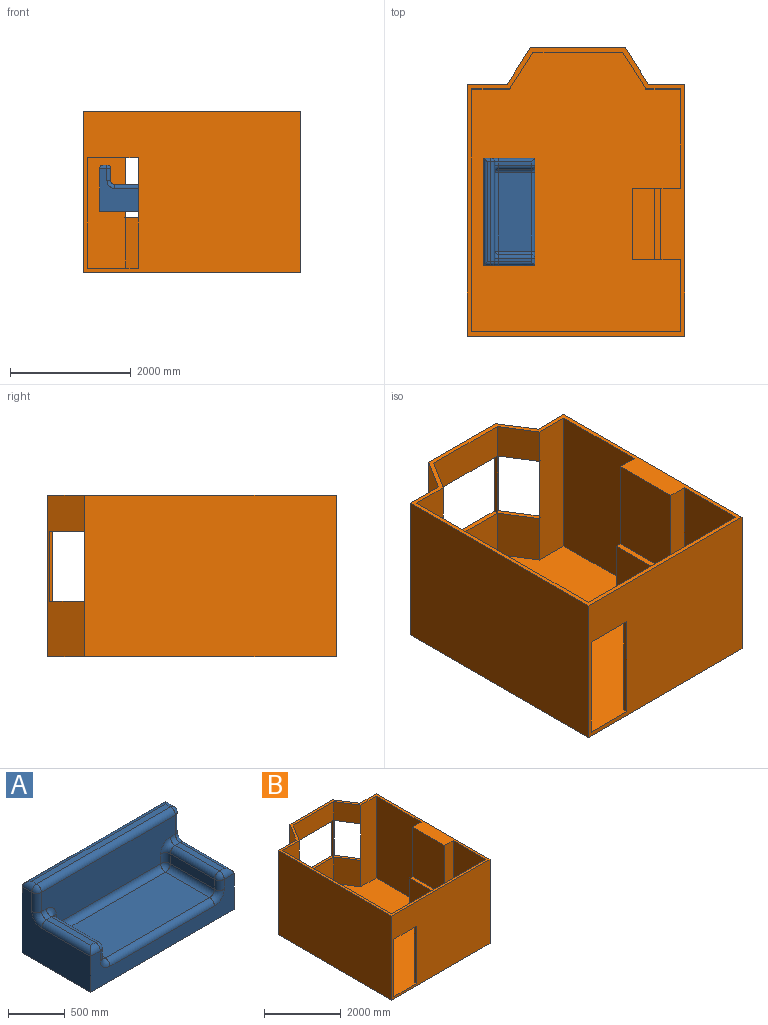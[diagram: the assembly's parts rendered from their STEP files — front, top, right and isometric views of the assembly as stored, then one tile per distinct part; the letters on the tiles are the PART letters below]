
ASSEMBLY  parts=2 mates=1
PART A: 46 faces, bbox 1780x850x770 mm
  f0: plane 1660x430.77mm, normal (0,-1,0), area 639255.4mm2, adj f17,f18,f22,f26,f30,f34,f38,f39
  f1: plane 548.57x61.43mm, normal (0,0,1), area 33697.9mm2, adj f13,f19,f22,f23
  f2: plane 1780x385.23mm, normal (0,-1,0), area 344493.1mm2, adj f3,f6,f7,f12,f15,f19,f20,f24
  f3: plane 1780x850mm, normal (0,0,-1), area 1513000mm2, adj f2,f4,f6,f7
  f4: plane 1780x710mm, normal (0,1,0), area 1263800mm2, adj f3,f6,f7,f36
  f5: plane 1660x61.43mm, normal (0,0,1), area 101971.3mm2, adj f31,f36,f39,f40
  f6: plane 850x710mm, normal (1,0,0), area 369971.1mm2, adj f2,f3,f4,f40,f41,f44,f45
  f7: plane 850x710mm, normal (-1,0,0), area 369971.1mm2, adj f2,f3,f4,f23,f27,f30,f31
  f8: plane 548.57x61.43mm, normal (0,0,1), area 33697.9mm2, adj f33,f37,f41,f42
  f9: plane 548.57x106mm, normal (1,0,0), area 58148.6mm2, adj f12,f13,f16,f17
  f10: plane 548.57x106mm, normal (-1,0,0), area 58148.6mm2, adj f25,f28,f33,f34
  f11: plane 1297.14x548.57mm, normal (0,0,1), area 711575.8mm2, adj f16,f20,f25,f26
  f12: cylinder r=60mm len=106mm, axis (0,0,1), area 9990.3mm2, adj f2,f9,f14,f15
  f13: cylinder r=60mm len=548.57mm, axis (0,-1,0), area 51701.6mm2, adj f1,f9,f14,f18
  f14: sphere r=60mm, area 5654.9mm2, adj f12,f13,f19
  f15: torus R=120mm, axis (0,1,0), area 12110.4mm2, adj f2,f12,f16,f20
  f16: cylinder r=60mm len=548.57mm, axis (0,1,0), area 51701.6mm2, adj f9,f11,f15,f21
  f17: cylinder r=60mm len=106mm, axis (0,0,-1), area 9990.3mm2, adj f0,f9,f18,f21
  f18: torus R=120mm, axis (0,1,0), area 12110.4mm2, adj f0,f13,f17,f22
  f19: cylinder r=60mm len=121.43mm, axis (-1,0,0), area 9389.5mm2, adj f1,f2,f14,f23
  f20: cylinder r=60mm len=1297.14mm, axis (1,0,0), area 122252.9mm2, adj f2,f11,f15,f24
  f21: sphere r=60mm, area 5654.9mm2, adj f16,f17,f26
  f22: cylinder r=60mm len=61.43mm, axis (1,0,0), area 5789.5mm2, adj f0,f1,f18,f27
  f23: cylinder r=60mm len=608.57mm, axis (0,1,0), area 55301.6mm2, adj f1,f7,f19,f27
  f24: torus R=120mm, axis (0,1,0), area 12110.4mm2, adj f2,f20,f25,f28
  f25: cylinder r=60mm len=548.57mm, axis (0,-1,0), area 51701.6mm2, adj f10,f11,f24,f29
  f26: cylinder r=60mm len=1297.14mm, axis (1,0,0), area 122252.9mm2, adj f0,f11,f21,f29
  f27: torus R=120mm, axis (-1,0,0), area 12110.4mm2, adj f7,f22,f23,f30
  f28: cylinder r=60mm len=106mm, axis (0,0,1), area 9990.3mm2, adj f2,f10,f24,f32
  f29: sphere r=60mm, area 5654.9mm2, adj f25,f26,f34
  f30: cylinder r=60mm len=204.77mm, axis (0,0,1), area 19299.3mm2, adj f0,f7,f27,f35
  f31: cylinder r=60mm len=121.43mm, axis (0,1,0), area 9389.5mm2, adj f5,f7,f35,f36
  f32: sphere r=60mm, area 5654.9mm2, adj f28,f33,f37
  f33: cylinder r=60mm len=548.57mm, axis (0,1,0), area 51701.6mm2, adj f8,f10,f32,f38
  f34: cylinder r=60mm len=106mm, axis (0,0,-1), area 9990.3mm2, adj f0,f10,f29,f38
  f35: sphere r=60mm, area 5654.9mm2, adj f30,f31,f39
  f36: cylinder r=60mm len=1780mm, axis (-1,0,0), area 163651.3mm2, adj f4,f5,f31,f40
  f37: cylinder r=60mm len=121.43mm, axis (-1,0,0), area 9389.5mm2, adj f2,f8,f32,f41
  f38: torus R=120mm, axis (0,1,0), area 12110.4mm2, adj f0,f33,f34,f42
  f39: cylinder r=60mm len=1660mm, axis (-1,0,0), area 156451.3mm2, adj f0,f5,f35,f43
  f40: cylinder r=60mm len=121.43mm, axis (0,-1,0), area 9389.5mm2, adj f5,f6,f36,f43
  f41: cylinder r=60mm len=608.57mm, axis (0,-1,0), area 55301.6mm2, adj f6,f8,f37,f44
  f42: cylinder r=60mm len=61.43mm, axis (1,0,0), area 5789.5mm2, adj f0,f8,f38,f44
  f43: sphere r=60mm, area 5654.9mm2, adj f39,f40,f45
  f44: torus R=120mm, axis (-1,0,0), area 12110.4mm2, adj f6,f41,f42,f45
  f45: cylinder r=60mm len=204.77mm, axis (0,0,-1), area 19299.3mm2, adj f0,f6,f43,f44
PART B: 46 faces, bbox 3610x4788.4x2675 mm
  f0: plane 4788.42x3610mm, normal (0,0,1), area 1573850mm2, adj f5,f7,f8,f9,f10,f11,f12,f13
  f1: plane 370x30mm, normal (0,1,0), area 11100mm2, adj f4,f20,f42,f43
  f2: plane 370x30mm, normal (0,-1,0), area 11100mm2, adj f4,f19,f42,f43
  f3: plane 1180x1000mm, normal (-1,0,0), area 1180000mm2, adj f19,f20,f43,f44
  f4: plane 4713.42x3460mm, normal (0,0,1), area 14215012.7mm2, adj f1,f2,f6,f8,f17,f18,f19,f20
  f5: plane 608.42x596.82mm, normal (-0.85,-0.53,0), area 429712.7mm2, adj f0,f7,f22,f40
  f6: plane 840x608.42mm, normal (0.85,-0.53,0), area 604797.1mm2, adj f4,f24,f26,f36
  f7: plane 1490x596.82mm, normal (0,-1,0), area 889266.5mm2, adj f0,f5,f25,f31
  f8: plane 3610x2675mm, normal (0,-1,0), area 8129702mm2, adj f0,f4,f9,f15,f16,f27,f28,f29
  f9: plane 4180x2675mm, normal (1,0,0), area 11181500mm2, adj f0,f8,f10,f16
  f10: plane 2675x603.7mm, normal (0,1,0), area 1525079.6mm2, adj f0,f9,f11,f16,f38,f40,f41
  f11: plane 2675x608.42mm, normal (0.85,0.53,0), area 1136543.9mm2, adj f0,f10,f12,f16,f39,f40,f41
  f12: plane 2675x1572.59mm, normal (0,1,0), area 2473541.3mm2, adj f0,f11,f13,f16,f30,f31,f32,f33
  f13: plane 2675x608.42mm, normal (-0.85,0.53,0), area 1136543.9mm2, adj f0,f12,f14,f16,f35,f36,f37
  f14: plane 2675x663.7mm, normal (0,1,0), area 1685579.6mm2, adj f0,f13,f15,f16,f34,f36,f37
  f15: plane 4180x2675mm, normal (-1,0,0), area 11181500mm2, adj f0,f8,f14,f16
  f16: plane 4788.42x3610mm, normal (0,0,-1), area 16280837.7mm2, adj f8,f9,f10,f11,f12,f13,f14,f15
  f17: plane 3460x2600mm, normal (0,1,0), area 7468952mm2, adj f0,f4,f18,f27,f28,f29
  f18: plane 2600x1200mm, normal (-1,0,0), area 3120000mm2, adj f0,f4,f17,f19
  f19: plane 2600x420mm, normal (0,-1,0), area 935000mm2, adj f0,f2,f3,f4,f18,f44,f45
  f20: plane 2600x420mm, normal (0,1,0), area 935000mm2, adj f0,f1,f3,f4,f21,f44,f45
  f21: plane 2600x1650mm, normal (-1,0,0), area 4290000mm2, adj f0,f4,f20,f22
  f22: plane 2600x570mm, normal (0,-1,0), area 1482000mm2, adj f0,f4,f5,f21,f23,f38
  f23: plane 840x608.42mm, normal (-0.85,-0.53,0), area 604797.1mm2, adj f4,f22,f24,f41
  f24: plane 1490x840mm, normal (0,-1,0), area 1251594mm2, adj f4,f6,f23,f33
  f25: plane 608.42x596.82mm, normal (0.85,-0.53,0), area 429712.7mm2, adj f0,f7,f26,f37
  f26: plane 2600x630mm, normal (0,-1,0), area 1638000mm2, adj f0,f4,f6,f25,f27,f34
  f27: plane 4105x2600mm, normal (1,0,0), area 10615160mm2, adj f0,f4,f8,f17,f26,f29
  f28: plane 1828.8x75mm, normal (-1,0,0), area 137160mm2, adj f4,f8,f17,f29
  f29: plane 835x75mm, normal (0,0,-1), area 62625mm2, adj f8,f17,f27,f28
  f30: plane 1163.18x75mm, normal (1,0,0), area 87238.6mm2, adj f12,f31,f33,f35
  f31: plane 1490x75mm, normal (0,0,-1), area 111750mm2, adj f7,f12,f30,f32
  f32: plane 1163.18x75mm, normal (-1,0,0), area 87238.6mm2, adj f12,f31,f33,f39
  f33: plane 1490x75mm, normal (0,0,1), area 111750mm2, adj f12,f24,f30,f32
  f34: plane 1163.18x118.52mm, normal (0.53,0.85,0), area 163147.4mm2, adj f14,f26,f36,f37
  f35: plane 1163.18x63.38mm, normal (-0.53,-0.85,0), area 87238.6mm2, adj f13,f30,f36,f37
  f36: plane 648.52x503.52mm, normal (0,0,1), area 55347.5mm2, adj f6,f13,f14,f34,f35
  f37: plane 648.52x503.52mm, normal (0,0,-1), area 55347.5mm2, adj f13,f14,f25,f34,f35
  f38: plane 1163.18x118.52mm, normal (-0.53,0.85,0), area 163147.4mm2, adj f10,f22,f40,f41
  f39: plane 1163.18x63.38mm, normal (0.53,-0.85,0), area 87238.6mm2, adj f11,f32,f40,f41
  f40: plane 648.52x503.52mm, normal (0,0,-1), area 55347.5mm2, adj f5,f10,f11,f38,f39
  f41: plane 648.52x503.52mm, normal (0,0,1), area 55347.5mm2, adj f10,f11,f23,f38,f39
  f42: plane 1180x30mm, normal (-1,0,0), area 35400mm2, adj f1,f2,f4,f43
  f43: plane 1180x370mm, normal (0,0,1), area 436600mm2, adj f1,f2,f3,f42
  f44: plane 1180x100mm, normal (0,0,1), area 118000mm2, adj f3,f19,f20,f45
  f45: plane 1570x1180mm, normal (-1,0,0), area 1852600mm2, adj f0,f19,f20,f44
PLACE A rot(axis=(0,0,1),90deg) t=(-591,-216.68,940.02)mm
PLACE B t=(-1639.08,-2205.16,0)mm fixed
MATE slider A.f4 <-> B.f27  axis (-1,0,0) through (-1441,-216.68,1295.02)mm
